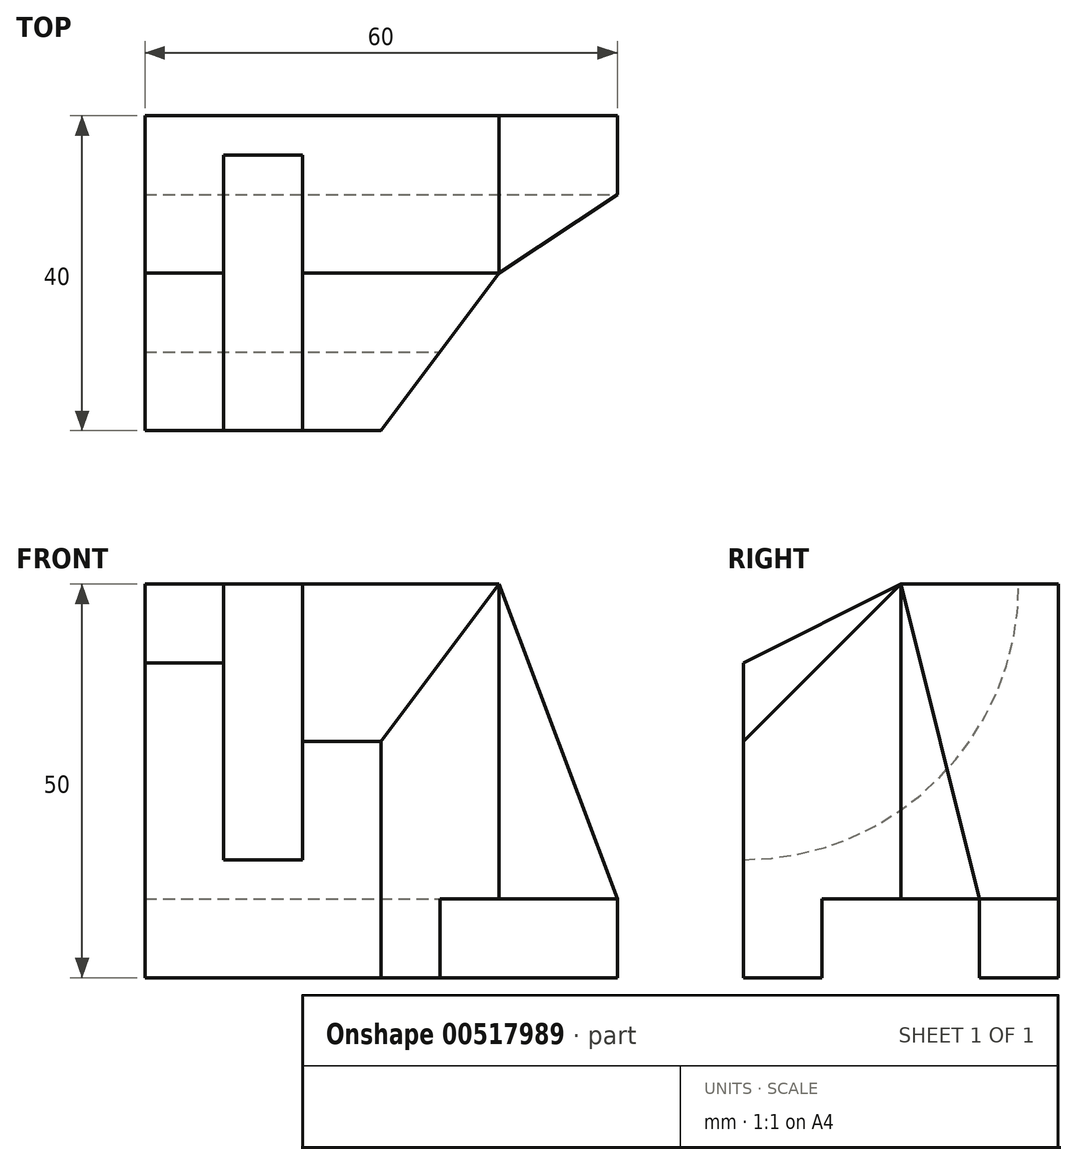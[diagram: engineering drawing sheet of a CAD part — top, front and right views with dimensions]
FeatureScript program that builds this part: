
annotation { "Feature Type Name" : "Feature", "Feature Type Description" : "" }
export const myFeature = defineFeature(function(context is Context, id is Id, definition is map)
    precondition{}
    {
        {
            var Q0;
            Q0=qCreatedBy(makeId("Top.planeOp"),FACE);
            var sketch = newSketch(context, id + "F0", { "sketchPlane" : qUnion([Q0])});
            skLineSegment(sketch, "E0.bottom", {"start": v(0, 0) * mm, "end": v(60, 0) * mm});
            skLineSegment(sketch, "E0.top", {"start": v(0, 40) * mm, "end": v(60, 40) * mm});
            skLineSegment(sketch, "E0.left", {"start": v(0, 0) * mm, "end": v(0, 40) * mm});
            skLineSegment(sketch, "E0.right", {"start": v(60, 0) * mm, "end": v(60, 40) * mm});
            skSolve(sketch);
        }
        {
            var Q0;
            Q0=makeQuery(id+"F0.imprint","IMPRINT",FACE,{"disambiguationData":[TD([[makeQuery(id+"F0.imprint","IMPRINT",EDGE,{"derivedFrom":sQuery(id+"F0.wireOp",EDGE,"E0.bottom")}),1.0]])]});
            extrude(context, id + "F1", {"entities" : qUnion([Q0]), "depth" : 50 * mm, "offsetDistance" : 25 * mm});
        }
        {
            var Q0;
            Q0=makeQuery(id+"F1.opExtrude","CAP_FACE",FACE,{"disambiguationData":[OSD([sQuery(id+"F0.wireOp",EDGE,"E0.bottom"),sQuery(id+"F0.wireOp",EDGE,"E0.top"),sQuery(id+"F0.wireOp",EDGE,"E0.left"),sQuery(id+"F0.wireOp",EDGE,"E0.right")])],"isStart":false});
            var sketch = newSketch(context, id + "F2", { "sketchPlane" : qUnion([Q0])});
            skLineSegment(sketch, "E1.bottom", {"start": v(10, 35) * mm, "end": v(20, 35) * mm});
            skLineSegment(sketch, "E1.top", {"start": v(10, 0) * mm, "end": v(20, 0) * mm});
            skLineSegment(sketch, "E1.left", {"start": v(10, 35) * mm, "end": v(10, 0) * mm});
            skLineSegment(sketch, "E1.right", {"start": v(20, 35) * mm, "end": v(20, 0) * mm});
            skSolve(sketch);
        }
        {
            var Q0;
            Q0=makeQuery(id+"F2.imprint","IMPRINT",FACE,{"disambiguationData":[TD([[makeQuery(id+"F2.imprint","IMPRINT",EDGE,{"derivedFrom":sQuery(id+"F2.wireOp",EDGE,"E1.bottom")}),-1.0]])]});
            extrude(context, id + "F3", {"entities" : qUnion([Q0]), "operationType" : NewBodyOperationType.REMOVE, "oppositeDirection" : true, "depth" : 35 * mm, "offsetDistance" : 25 * mm});
        }
        {
            var Q0;
            Q0=makeQuery(id+"F3.boolean.opBoolean","COPY",EDGE,{"derivedFrom":makeQuery(id+"F3.opExtrude","CAP_EDGE",EDGE,{"disambiguationData":[OSD([sQuery(id+"F2.wireOp",EDGE,"E1.bottom")])],"isStart":false})});
            fillet(context, id + "F4", {"entities" : qUnion([Q0]), "radius" : 35 * mm, "tangentPropagation" : true, "allowEdgeOverflow" : false});
        }
        {
            var Q0;
            Q0=makeQuery(id+"F1.opExtrude","SWEPT_FACE",FACE,{"disambiguationData":[OSD([sQuery(id+"F0.wireOp",EDGE,"E0.right")])]});
            var sketch = newSketch(context, id + "F5", { "sketchPlane" : qUnion([Q0])});
            skLineSegment(sketch, "E2.bottom", {"start": v(10, 0) * mm, "end": v(30, 0) * mm});
            skLineSegment(sketch, "E2.top", {"start": v(10, 10) * mm, "end": v(30, 10) * mm});
            skLineSegment(sketch, "E2.left", {"start": v(10, 0) * mm, "end": v(10, 10) * mm});
            skLineSegment(sketch, "E2.right", {"start": v(30, 0) * mm, "end": v(30, 10) * mm});
            skSolve(sketch);
        }
        {
            var Q0;
            Q0=makeQuery(id+"F5.imprint","IMPRINT",FACE,{"disambiguationData":[TD([[makeQuery(id+"F5.imprint","IMPRINT",EDGE,{"derivedFrom":sQuery(id+"F5.wireOp",EDGE,"E2.bottom")}),1.0]])]});
            extrude(context, id + "F6", {"entities" : qUnion([Q0]), "operationType" : NewBodyOperationType.REMOVE, "endBound" : BoundingType.THROUGH_ALL, "oppositeDirection" : true, "depth" : 25 * mm, "offsetDistance" : 25 * mm});
        }
        {
            var Q0;
            Q0=makeQuery(id+"F1.opExtrude","CAP_FACE",FACE,{"disambiguationData":[OSD([sQuery(id+"F0.wireOp",EDGE,"E0.bottom"),sQuery(id+"F0.wireOp",EDGE,"E0.top"),sQuery(id+"F0.wireOp",EDGE,"E0.left"),sQuery(id+"F0.wireOp",EDGE,"E0.right")])],"isStart":false});
            var sketch = newSketch(context, id + "F7", { "sketchPlane" : qUnion([Q0])});
            skLineSegment(sketch, "E3.bottom", {"start": v(0, 20) * mm, "end": v(10, 20) * mm});
            skLineSegment(sketch, "E3.top", {"start": v(0, 0) * mm, "end": v(10, 0) * mm});
            skLineSegment(sketch, "E3.left", {"start": v(0, 20) * mm, "end": v(0, 0) * mm});
            skLineSegment(sketch, "E3.right", {"start": v(10, 20) * mm, "end": v(10, 0) * mm});
            skSolve(sketch);
        }
        {
            var Q0;
            Q0=makeQuery(id+"F1.opExtrude","SWEPT_FACE",FACE,{"disambiguationData":[OSD([sQuery(id+"F0.wireOp",EDGE,"E0.left")])]});
            var sketch = newSketch(context, id + "F8", { "sketchPlane" : qUnion([Q0])});
            skLineSegment(sketch, "E4", {"start": v(-20, 50) * mm, "end": v(0, 40) * mm});
            skSolve(sketch);
        }
        {
            var Q0;
            Q0=makeQuery(id+"F7.imprint","IMPRINT",FACE,{"disambiguationData":[TD([[makeQuery(id+"F7.imprint","IMPRINT",EDGE,{"derivedFrom":sQuery(id+"F7.wireOp",EDGE,"E3.bottom")}),-1.0]])]});
            var Q1;
            Q1=sQuery(id+"F8.wireOp",EDGE,"E4");
            sweep(context, id + "F9", {"operationType" : NewBodyOperationType.REMOVE, "profiles" : qUnion([Q0]), "path" : qUnion([Q1])});
        }
        {
            var Q0;
            Q0=makeQuery(id+"F1.opExtrude","CAP_FACE",FACE,{"disambiguationData":[OSD([sQuery(id+"F0.wireOp",EDGE,"E0.bottom"),sQuery(id+"F0.wireOp",EDGE,"E0.top"),sQuery(id+"F0.wireOp",EDGE,"E0.left"),sQuery(id+"F0.wireOp",EDGE,"E0.right")])],"isStart":false});
            var sketch = newSketch(context, id + "F10", { "sketchPlane" : qUnion([Q0])});
            skLineSegment(sketch, "E5.bottom", {"start": v(60, 0) * mm, "end": v(45, 0) * mm});
            skLineSegment(sketch, "E5.top", {"start": v(60, 20) * mm, "end": v(45, 20) * mm});
            skLineSegment(sketch, "E5.left", {"start": v(60, 0) * mm, "end": v(60, 20) * mm});
            skLineSegment(sketch, "E5.right", {"start": v(45, 0) * mm, "end": v(45, 20) * mm});
            skSolve(sketch);
        }
        {
            var Q0;
            Q0=makeQuery(id+"F10.imprint","IMPRINT",FACE,{"disambiguationData":[TD([[makeQuery(id+"F10.imprint","IMPRINT",EDGE,{"derivedFrom":sQuery(id+"F10.wireOp",EDGE,"E5.bottom")}),1.0]])]});
            extrude(context, id + "F11", {"entities" : qUnion([Q0]), "operationType" : NewBodyOperationType.REMOVE, "endBound" : BoundingType.THROUGH_ALL, "oppositeDirection" : true, "depth" : 25 * mm, "offsetDistance" : 25 * mm});
        }
        {
            var Q0;
            Q0=makeQuery(id+"F1.opExtrude","CAP_FACE",FACE,{"disambiguationData":[OSD([sQuery(id+"F0.wireOp",EDGE,"E0.bottom"),sQuery(id+"F0.wireOp",EDGE,"E0.top"),sQuery(id+"F0.wireOp",EDGE,"E0.left"),sQuery(id+"F0.wireOp",EDGE,"E0.right")])],"isStart":false});
            var sketch = newSketch(context, id + "F12", { "sketchPlane" : qUnion([Q0])});
            skLineSegment(sketch, "E6", {"start": v(45, 20) * mm, "end": v(30, 0) * mm});
            skSolve(sketch);
        }
        {
            var Q0;
            {var subQ0=sQuery(id+"F12.wireOp",EDGE,"E6");Q0=makeQuery(id+"F12.imprint","IMPRINT",FACE,{"disambiguationData":[TD([[makeQuery(id+"F12.imprint","IMPRINT",EDGE,{"derivedFrom":subQ0}),1.0]])]});}
            extrude(context, id + "F13", {"entities" : qUnion([Q0]), "operationType" : NewBodyOperationType.REMOVE, "endBound" : BoundingType.THROUGH_ALL, "oppositeDirection" : true, "depth" : 25 * mm, "offsetDistance" : 25 * mm});
        }
        {
            var Q0;
            Q0=makeQuery(id+"F1.opExtrude","CAP_FACE",FACE,{"disambiguationData":[OSD([sQuery(id+"F0.wireOp",EDGE,"E0.bottom"),sQuery(id+"F0.wireOp",EDGE,"E0.top"),sQuery(id+"F0.wireOp",EDGE,"E0.left"),sQuery(id+"F0.wireOp",EDGE,"E0.right")])],"isStart":false});
            var sketch = newSketch(context, id + "F14", { "sketchPlane" : qUnion([Q0])});
            skLineSegment(sketch, "E7", {"start": v(45, 20) * mm, "end": v(20, 20) * mm});
            skPoint(sketch, "E7.endSnap0", {"position": v(20, 17.5) * mm});
            skSolve(sketch);
        }
        {
            var Q0;
            Q0=makeQuery(id+"F3.boolean.opBoolean","COPY",FACE,{"derivedFrom":makeQuery(id+"F3.opExtrude","SWEPT_FACE",FACE,{"disambiguationData":[OSD([sQuery(id+"F2.wireOp",EDGE,"E1.right")])]})});
            var sketch = newSketch(context, id + "F15", { "sketchPlane" : qUnion([Q0])});
            skLineSegment(sketch, "E8", {"start": v(-20, 50) * mm, "end": v(0, 30) * mm});
            skSolve(sketch);
        }
        {
            var Q0;
            {var subQ0=sQuery(id+"F14.wireOp",EDGE,"E7");Q0=makeQuery(id+"F14.imprint","IMPRINT",FACE,{"disambiguationData":[TD([[makeQuery(id+"F14.imprint","IMPRINT",EDGE,{"derivedFrom":subQ0}),1.0]])]});}
            var Q1;
            Q1=sQuery(id+"F15.wireOp",EDGE,"E8");
            sweep(context, id + "F16", {"operationType" : NewBodyOperationType.REMOVE, "profiles" : qUnion([Q0]), "path" : qUnion([Q1])});
        }
        {
            var Q0;
            Q0=makeQuery(id+"F1.opExtrude","CAP_FACE",FACE,{"disambiguationData":[OSD([sQuery(id+"F0.wireOp",EDGE,"E0.bottom"),sQuery(id+"F0.wireOp",EDGE,"E0.top"),sQuery(id+"F0.wireOp",EDGE,"E0.left"),sQuery(id+"F0.wireOp",EDGE,"E0.right")])],"isStart":false});
            var sketch = newSketch(context, id + "F17", { "sketchPlane" : qUnion([Q0])});
            skLineSegment(sketch, "E9", {"start": v(45, 20) * mm, "end": v(45, 40) * mm});
            skSolve(sketch);
        }
        {
            var Q0;
            Q0=makeQuery(id+"F1.opExtrude","SWEPT_FACE",FACE,{"disambiguationData":[OSD([sQuery(id+"F0.wireOp",EDGE,"E0.top")])]});
            var sketch = newSketch(context, id + "F18", { "sketchPlane" : qUnion([Q0])});
            skLineSegment(sketch, "E10", {"start": v(-45, 50) * mm, "end": v(-60, 10) * mm});
            skSolve(sketch);
        }
        {
            var Q0;
            {var subQ0=sQuery(id+"F17.wireOp",EDGE,"E9");Q0=makeQuery(id+"F17.imprint","IMPRINT",FACE,{"disambiguationData":[TD([[makeQuery(id+"F17.imprint","IMPRINT",EDGE,{"derivedFrom":subQ0}),-1.0]])]});}
            var Q1;
            Q1=sQuery(id+"F18.wireOp",EDGE,"E10");
            sweep(context, id + "F19", {"operationType" : NewBodyOperationType.REMOVE, "profiles" : qUnion([Q0]), "path" : qUnion([Q1])});
        }
        {
            var Q0;
            Q0=makeQuery(id+"F6.boolean.opBoolean","COPY",VERTEX,{"derivedFrom":makeQuery(id+"F6.opExtrude","CAP_VERTEX",VERTEX,{"disambiguationData":[OSD([sQuery(id+"F5.wireOp",EDGE,"E2.top"),sQuery(id+"F5.wireOp",EDGE,"E2.right")])],"isStart":true})});
            var Q1;
            Q1=makeQuery(id+"F11.boolean.opBoolean","INTERSECT",VERTEX,{"derivedFrom":[makeQuery(id+"F6.boolean.opBoolean","COPY",FACE,{"derivedFrom":makeQuery(id+"F6.opExtrude","SWEPT_FACE",FACE,{"disambiguationData":[OSD([sQuery(id+"F5.wireOp",EDGE,"E2.top")])]})}),makeQuery(id+"F11.opExtrude","SWEPT_FACE",FACE,{"disambiguationData":[OSD([sQuery(id+"F10.wireOp",EDGE,"E5.top")])]}),makeQuery(id+"F11.opExtrude","SWEPT_FACE",FACE,{"disambiguationData":[OSD([sQuery(id+"F10.wireOp",EDGE,"E5.right")])]})]});
            var Q2;
            {var subQ0=sQuery(id+"F14.wireOp",EDGE,"E7");var subQ1=sQuery(id+"F10.wireOp",EDGE,"E5.top");var subQ2=sQuery(id+"F12.wireOp",EDGE,"E6");var subQ3=sQuery(id+"F10.wireOp",EDGE,"E5.right");Q2=makeQuery(id+"F19.boolean.opBoolean","MERGE",VERTEX,{"derivedFrom":[makeQuery(id+"F16.boolean.opBoolean","MERGE",VERTEX,{"derivedFrom":[makeQuery(id+"F13.boolean.opBoolean","MERGE",VERTEX,{"derivedFrom":[makeQuery(id+"F11.boolean.opBoolean","COPY",VERTEX,{"derivedFrom":makeQuery(id+"F11.opExtrude","CAP_VERTEX",VERTEX,{"disambiguationData":[OSD([subQ1,subQ3])],"isStart":true})}),makeQuery(id+"F13.opExtrude","CAP_VERTEX",VERTEX,{"disambiguationData":[OSD([subQ1,subQ3,subQ2])],"isStart":true})]}),makeQuery(id+"F16.opSweep","CAP_VERTEX",VERTEX,{"disambiguationData":[OSD([subQ1,subQ2,subQ0,sQuery(id+"F15.wireOp",EDGE,"E8")])],"isStart":true})]}),makeQuery(id+"F19.opSweep","CAP_VERTEX",VERTEX,{"disambiguationData":[OSD([subQ1,subQ0,sQuery(id+"F15.wireOp",VERTEX,"E8.start"),sQuery(id+"F17.wireOp",EDGE,"E9"),sQuery(id+"F18.wireOp",EDGE,"E10")])],"isStart":true})]});}
            cPlane(context, id + "F20", {"entities" : qUnion([Q0, Q1, Q2]), "cplaneType" : CPlaneType.THREE_POINT, "offset" : 25 * mm, "width" : 150 * mm, "height" : 150 * mm});
        }
        {
            var Q0;
            Q0=makeQuery(id+"F19.boolean.opBoolean","COPY",FACE,{"derivedFrom":makeQuery(id+"F19.opSweep","SWEPT_FACE",FACE,{"disambiguationData":[OSD([sQuery(id+"F17.wireOp",EDGE,"E9"),sQuery(id+"F18.wireOp",EDGE,"E10")])]})});
            var sketch = newSketch(context, id + "F21", { "sketchPlane" : qUnion([Q0])});
            skLineSegment(sketch, "E11", {"start": v(30, -11.7) * mm, "end": v(20, 31.02) * mm});
            skSolve(sketch);
        }
        {
            var Q0;
            Q0=makeQuery(id+"F21.imprint","IMPRINT",FACE,{"disambiguationData":[TD([[makeQuery(id+"F21.imprint","IMPRINT",EDGE,{"derivedFrom":sQuery(id+"F21.wireOp",EDGE,"E11")}),1.0]])]});
            var Q1;
            Q1=qCreatedBy(id+"F20.planeOp",FACE);
            extrude(context, id + "F22", {"entities" : qUnion([Q0]), "operationType" : NewBodyOperationType.REMOVE, "endBound" : BoundingType.UP_TO_SURFACE, "oppositeDirection" : true, "depth" : 25 * mm, "endBoundEntityFace" : qUnion([Q1]), "offsetDistance" : 25 * mm});
        }
    });
